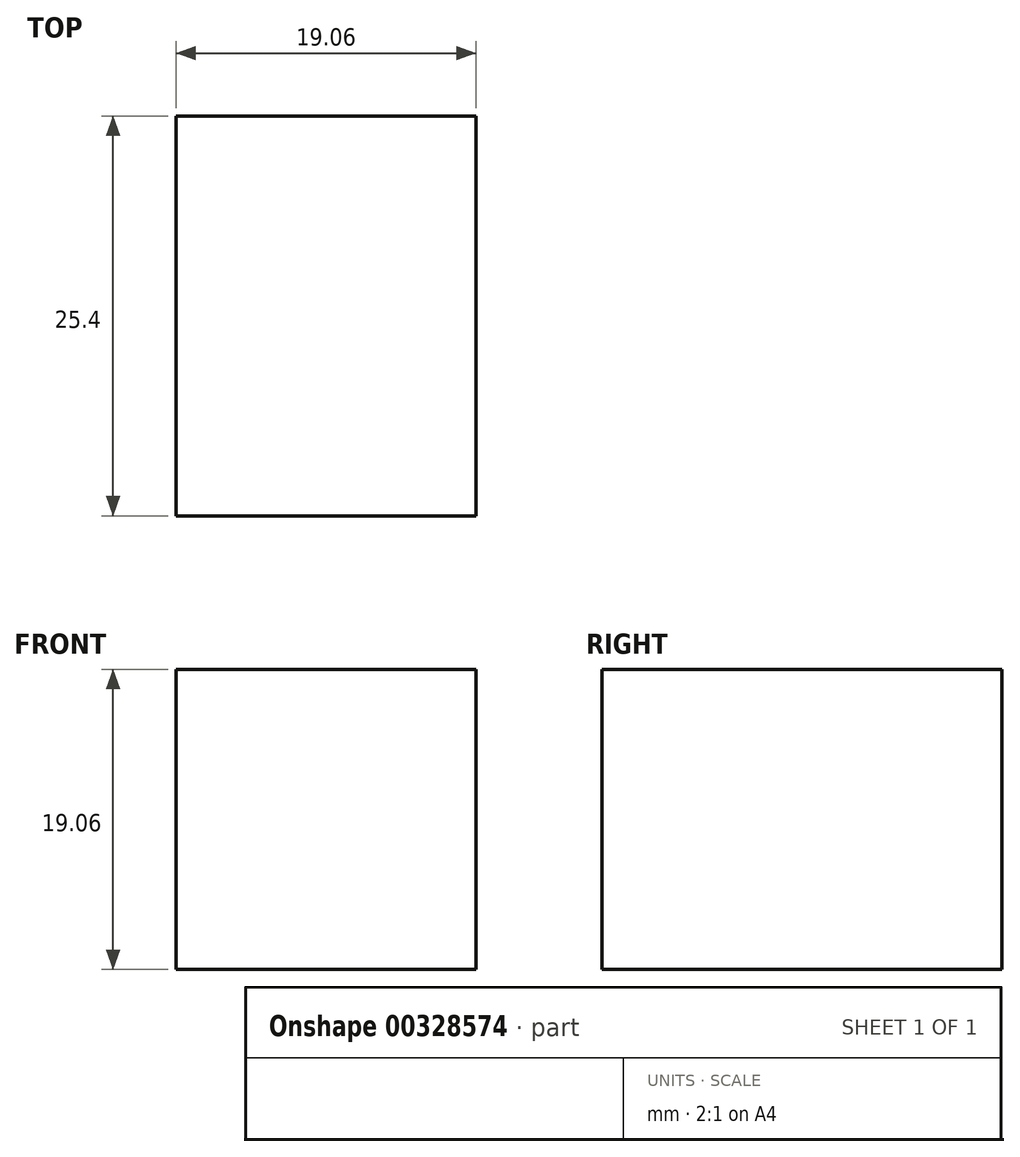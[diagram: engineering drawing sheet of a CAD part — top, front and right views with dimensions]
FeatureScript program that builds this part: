
annotation { "Feature Type Name" : "Feature", "Feature Type Description" : "" }
export const myFeature = defineFeature(function(context is Context, id is Id, definition is map)
    precondition{}
    {
        {
            var Q0;
            Q0=qCreatedBy(makeId("Front.planeOp"),FACE);
            var sketch = newSketch(context, id + "F0", { "sketchPlane" : qUnion([Q0])});
            skLineSegment(sketch, "E0.bottom", {"start": v(9.52, 9.53) * mm, "end": v(-9.53, 9.53) * mm});
            skLineSegment(sketch, "E0.top", {"start": v(9.53, -9.53) * mm, "end": v(-9.52, -9.53) * mm});
            skLineSegment(sketch, "E0.left", {"start": v(9.52, 9.53) * mm, "end": v(9.53, -9.53) * mm});
            skLineSegment(sketch, "E0.right", {"start": v(-9.53, 9.53) * mm, "end": v(-9.52, -9.53) * mm});
            skPoint(sketch, "E0.middle", {"position": v(0, 0) * mm});
            skSolve(sketch);
        }
        {
            var Q0;
            Q0 = qSketchRegion(id + "F0", true);
            extrude(context, id + "F1", {"entities" : qUnion([Q0]), "endBound" : BoundingType.SYMMETRIC, "depth" : 25.4 * mm});
        }
    });
